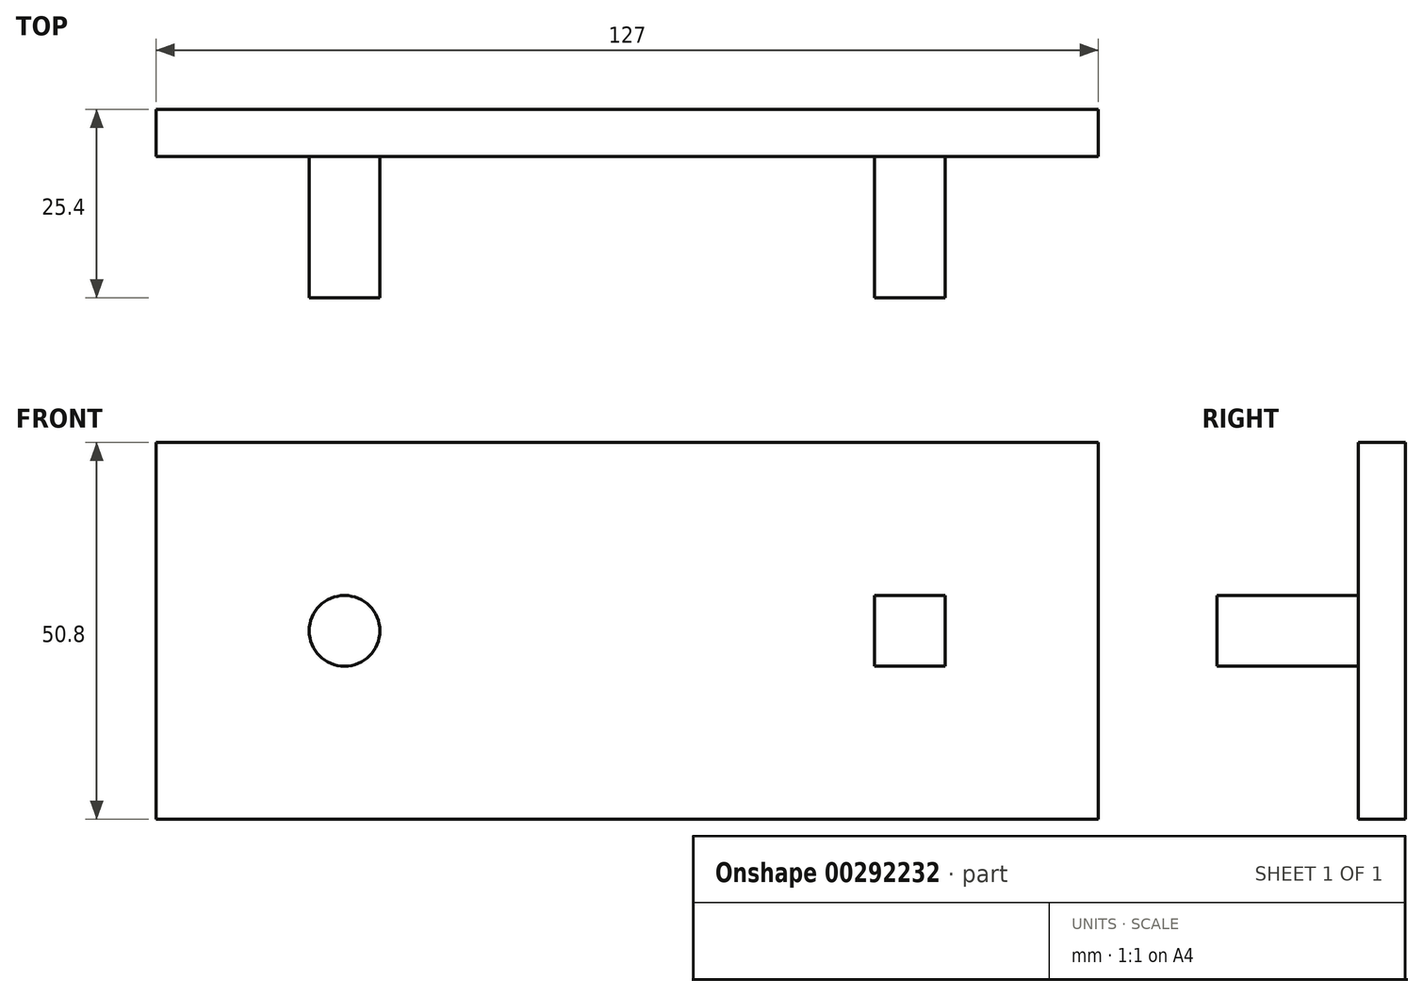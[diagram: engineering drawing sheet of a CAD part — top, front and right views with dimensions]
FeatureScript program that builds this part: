
annotation { "Feature Type Name" : "Feature", "Feature Type Description" : "" }
export const myFeature = defineFeature(function(context is Context, id is Id, definition is map)
    precondition{}
    {
        {
            var Q0;
            Q0=qCreatedBy(makeId("Front.planeOp"),FACE);
            var sketch = newSketch(context, id + "F0", { "sketchPlane" : qUnion([Q0])});
            skLineSegment(sketch, "E0.bottom", {"start": v(0, 0) * mm, "end": v(127, 0) * mm});
            skLineSegment(sketch, "E0.top", {"start": v(0, 50.8) * mm, "end": v(127, 50.8) * mm});
            skLineSegment(sketch, "E0.left", {"start": v(0, 0) * mm, "end": v(0, 50.8) * mm});
            skLineSegment(sketch, "E0.right", {"start": v(127, 0) * mm, "end": v(127, 50.8) * mm});
            skSolve(sketch);
        }
        {
            var Q0;
            Q0=makeQuery(id+"F0.imprint","IMPRINT",FACE,{"disambiguationData":[TD([[makeQuery(id+"F0.imprint","IMPRINT",EDGE,{"derivedFrom":sQuery(id+"F0.wireOp",EDGE,"E0.bottom")}),1.0]])]});
            extrude(context, id + "F1", {"entities" : qUnion([Q0]), "depth" : 6.35 * mm});
        }
        {
            var Q0;
            Q0=makeQuery(id+"F1.opExtrude","CAP_FACE",FACE,{"disambiguationData":[OSD([sQuery(id+"F0.wireOp",EDGE,"E0.bottom"),sQuery(id+"F0.wireOp",EDGE,"E0.top"),sQuery(id+"F0.wireOp",EDGE,"E0.left"),sQuery(id+"F0.wireOp",EDGE,"E0.right")])],"isStart":false});
            var sketch = newSketch(context, id + "F2", { "sketchPlane" : qUnion([Q0])});
            skLineSegment(sketch, "E1", {"start": v(0, 0) * mm, "end": v(0, 25.4) * mm});
            skLineSegment(sketch, "E2", {"start": v(0, 25.4) * mm, "end": v(25.4, 25.4) * mm});
            skCircle(sketch, "E3", {"center": v(25.4, 25.4) * mm, "radius": 4.76 * mm});
            skSolve(sketch);
        }
        {
            var Q0;
            Q0=makeQuery(id+"F2.imprint","IMPRINT",FACE,{"disambiguationData":[TD([[makeQuery(id+"F2.imprint","IMPRINT",EDGE,{"derivedFrom":sQuery(id+"F2.wireOp",EDGE,"E3")}),1.0]])]});
            extrude(context, id + "F3", {"entities" : qUnion([Q0]), "operationType" : NewBodyOperationType.ADD, "depth" : 19.05 * mm});
        }
        {
            var Q0;
            Q0=makeQuery(id+"F1.opExtrude","CAP_FACE",FACE,{"disambiguationData":[OSD([sQuery(id+"F0.wireOp",EDGE,"E0.bottom"),sQuery(id+"F0.wireOp",EDGE,"E0.top"),sQuery(id+"F0.wireOp",EDGE,"E0.left"),sQuery(id+"F0.wireOp",EDGE,"E0.right")])],"isStart":false});
            var sketch = newSketch(context, id + "F4", { "sketchPlane" : qUnion([Q0])});
            skLineSegment(sketch, "E4", {"start": v(127, 0) * mm, "end": v(127, 25.4) * mm});
            skLineSegment(sketch, "E5", {"start": v(127, 25.4) * mm, "end": v(101.59, 25.4) * mm});
            skLineSegment(sketch, "E6.bottom", {"start": v(96.83, 30.16) * mm, "end": v(106.35, 30.16) * mm});
            skLineSegment(sketch, "E6.top", {"start": v(96.83, 20.64) * mm, "end": v(106.35, 20.64) * mm});
            skLineSegment(sketch, "E6.left", {"start": v(96.83, 30.16) * mm, "end": v(96.83, 20.64) * mm});
            skLineSegment(sketch, "E6.right", {"start": v(106.35, 30.16) * mm, "end": v(106.35, 20.64) * mm});
            skPoint(sketch, "E6.middle", {"position": v(101.59, 25.4) * mm});
            skSolve(sketch);
        }
        {
            var Q0;
            {var subQ1=sQuery(id+"F4.wireOp",EDGE,"E6.bottom");Q0=makeQuery(id+"F4.imprint","IMPRINT",FACE,{"disambiguationData":[TD([[makeQuery(id+"F4.imprint","IMPRINT",EDGE,{"derivedFrom":subQ1}),-1.0]])]});}
            extrude(context, id + "F5", {"entities" : qUnion([Q0]), "operationType" : NewBodyOperationType.ADD, "depth" : 19.05 * mm});
        }
    });
